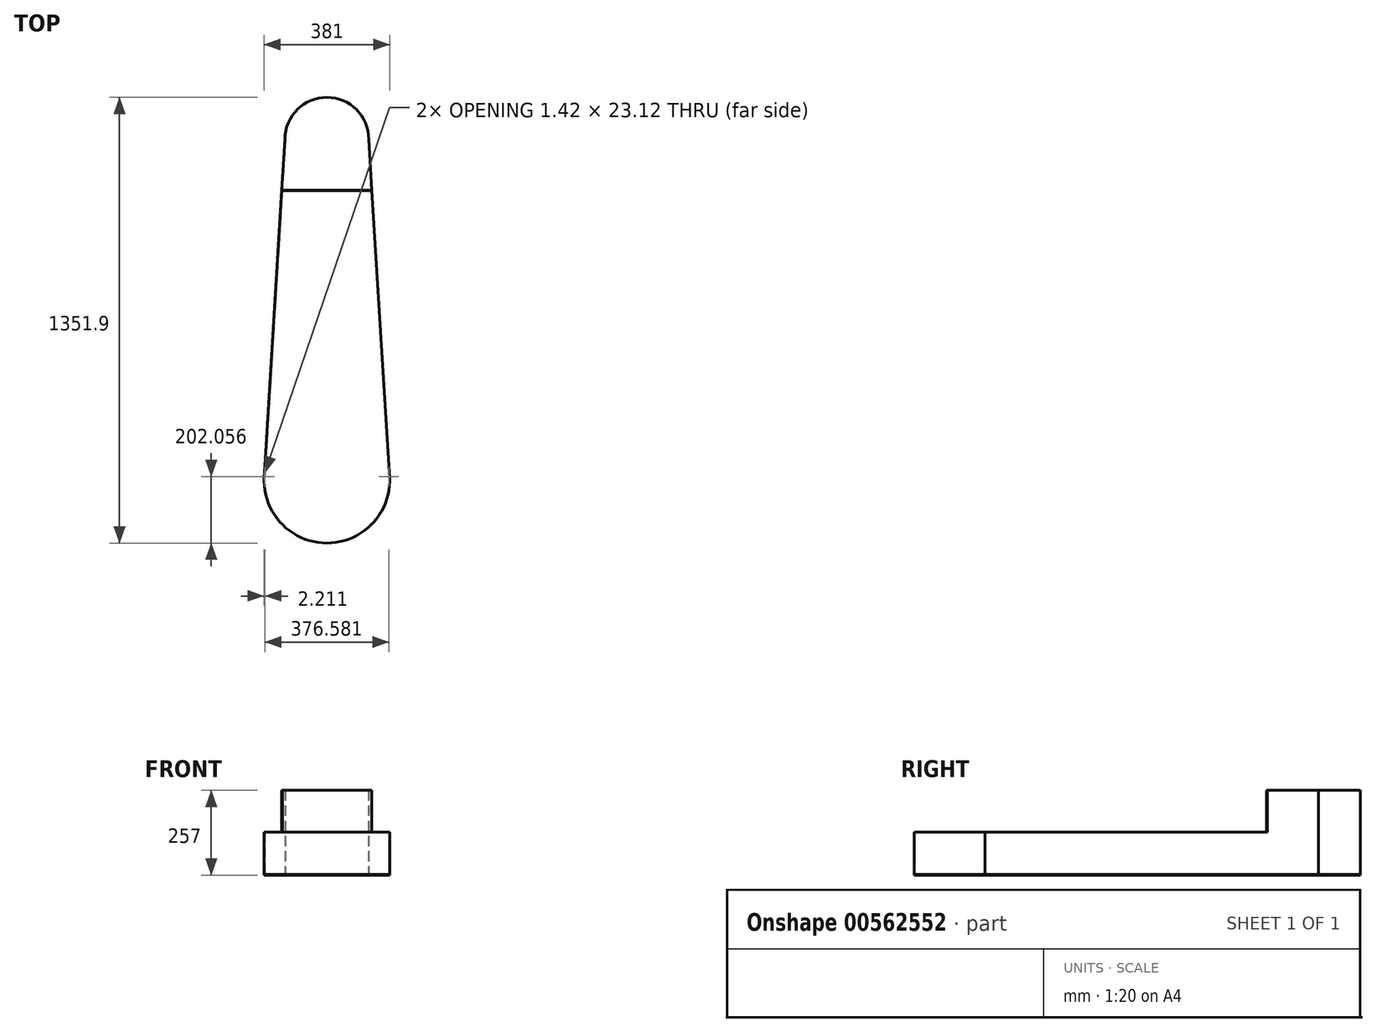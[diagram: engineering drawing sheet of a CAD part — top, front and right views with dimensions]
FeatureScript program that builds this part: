
annotation { "Feature Type Name" : "Feature", "Feature Type Description" : "" }
export const myFeature = defineFeature(function(context is Context, id is Id, definition is map)
    precondition{}
    {
        {
            var Q0;
            Q0=qCreatedBy(makeId("Top.planeOp"),FACE);
            var sketch = newSketch(context, id + "F0", { "sketchPlane" : qUnion([Q0])});
            skArc(sketch, "E0", {"start": v(142.28, 32.75) * mm, "mid": v(15.97, 172.96) * mm, "end": v(-110.34, 32.75) * mm});
            skArc(sketch, "E1", {"start": v(-170.7, -950.41) * mm, "mid": v(15.97, -1178.94) * mm, "end": v(202.64, -950.41) * mm});
            skLineSegment(sketch, "E2", {"start": v(-111.03, 45.96) * mm, "end": v(-174.53, -988.44) * mm});
            skLineSegment(sketch, "E3", {"start": v(142.97, 45.96) * mm, "end": v(206.47, -988.44) * mm});
            skArc(sketch, "E4", {"start": v(141.47, 45.96) * mm, "mid": v(15.97, 171.46) * mm, "end": v(-109.53, 45.96) * mm});
            skArc(sketch, "E5", {"start": v(-171.6, -965.33) * mm, "mid": v(15.97, -1177.44) * mm, "end": v(203.55, -965.33) * mm});
            skLineSegment(sketch, "E6", {"start": v(141.47, 45.96) * mm, "end": v(204.97, -988.44) * mm});
            skLineSegment(sketch, "E7", {"start": v(-109.53, 45.96) * mm, "end": v(-173.03, -988.44) * mm});
            skCircle(sketch, "E8", {"center": v(15.97, 45.96) * mm, "radius": 96.01 * mm});
            skCircle(sketch, "E9", {"center": v(15.97, -988.44) * mm, "radius": 149.65 * mm});
            skLineSegment(sketch, "E10", {"start": v(-120.54, -109.06) * mm, "end": v(-119.04, -109.06) * mm});
            skLineSegment(sketch, "E11", {"start": v(150.99, -109.06) * mm, "end": v(152.48, -108.97) * mm});
            skSolve(sketch);
        }
        {
            var Q0;
            {var subQ0=sQuery(id+"F0.wireOp",EDGE,"E4");Q0=makeQuery(id+"F0.imprint","IMPRINT",FACE,{"disambiguationData":[TD([[makeQuery(id+"F0.imprint","IMPRINT",EDGE,{"derivedFrom":subQ0}),-1.0]])]});}
            var Q1;
            {var subQ5=sQuery(id+"F0.wireOp",EDGE,"E10");Q1=makeQuery(id+"F0.imprint","IMPRINT",FACE,{"disambiguationData":[TD([[makeQuery(id+"F0.imprint","IMPRINT",EDGE,{"derivedFrom":subQ5}),1.0]])]});}
            var Q2;
            {var subQ5=sQuery(id+"F0.wireOp",EDGE,"E11");Q2=makeQuery(id+"F0.imprint","IMPRINT",FACE,{"disambiguationData":[TD([[makeQuery(id+"F0.imprint","IMPRINT",EDGE,{"derivedFrom":subQ5}),1.0]])]});}
            extrude(context, id + "F1", {"entities" : qUnion([Q0, Q1, Q2]), "depth" : 254 * mm, "offsetDistance" : 25.4 * mm});
        }
        {
            var Q0;
            Q0 = qSketchRegion(id + "F0", true);
            extrude(context, id + "F2", {"entities" : qUnion([Q0]), "operationType" : NewBodyOperationType.ADD, "depth" : 127 * mm, "offsetDistance" : 25.4 * mm});
        }
        {
            var Q0;
            Q0 = qSketchRegion(id + "F0", true);
            var Q1;
            {var subQ4=sQuery(id+"F0.wireOp",EDGE,"E4");Q1=makeQuery(id+"F0.imprint","IMPRINT",FACE,{"disambiguationData":[TD([[makeQuery(id+"F0.imprint","IMPRINT",EDGE,{"derivedFrom":subQ4}),1.0]])]});}
            var Q2;
            Q2=makeQuery(id+"F0.imprint","IMPRINT",FACE,{"disambiguationData":[TD([[makeQuery(id+"F0.imprint","IMPRINT",EDGE,{"derivedFrom":sQuery(id+"F0.wireOp",EDGE,"E9")}),1.0]])]});
            var Q3;
            Q3=makeQuery(id+"F0.imprint","IMPRINT",FACE,{"disambiguationData":[TD([[makeQuery(id+"F0.imprint","IMPRINT",EDGE,{"derivedFrom":sQuery(id+"F0.wireOp",EDGE,"E8")}),1.0]])]});
            extrude(context, id + "F3", {"entities" : qUnion([Q0, Q1, Q2, Q3]), "oppositeDirection" : true, "depth" : 1.5 * mm, "offsetDistance" : 25.4 * mm});
        }
        {
            var Q0;
            Q0=makeQuery(id+"F1.opExtrude","CAP_FACE",FACE,{"disambiguationData":[OSD([sQuery(id+"F0.wireOp",EDGE,"E0"),sQuery(id+"F0.wireOp",EDGE,"E2"),sQuery(id+"F0.wireOp",EDGE,"E3"),sQuery(id+"F0.wireOp",EDGE,"E4"),sQuery(id+"F0.wireOp",EDGE,"E6"),sQuery(id+"F0.wireOp",EDGE,"E7"),sQuery(id+"F0.wireOp",EDGE,"E10"),sQuery(id+"F0.wireOp",EDGE,"E11")])],"isStart":false});
            var sketch = newSketch(context, id + "F4", { "sketchPlane" : qUnion([Q0])});
            skLineSegment(sketch, "E12", {"start": v(-119.04, -109.06) * mm, "end": v(152.48, -108.97) * mm});
            skSolve(sketch);
        }
        {
            var Q0;
            {var subQ4=makeQuery(id+"F1.opExtrude","CAP_EDGE",EDGE,{"disambiguationData":[OSD([sQuery(id+"F0.wireOp",EDGE,"E4")])],"isStart":false});Q0=makeQuery(id+"F4.imprint","IMPRINT",FACE,{"disambiguationData":[TD([[makeQuery(id+"F4.imprint","IMPRINT",EDGE,{"derivedFrom":subQ4}),1.0]])]});}
            var Q1;
            Q1=makeQuery(id+"F4.imprint","IMPRINT",FACE,{"disambiguationData":[TD([[makeQuery(id+"F4.imprint","IMPRINT",EDGE,{"derivedFrom":makeQuery(id+"F1.opExtrude","CAP_EDGE",EDGE,{"disambiguationData":[OSD([sQuery(id+"F0.wireOp",EDGE,"E0")])],"isStart":false})}),1.0]])]});
            extrude(context, id + "F5", {"entities" : qUnion([Q0, Q1]), "operationType" : NewBodyOperationType.ADD, "depth" : 1.5 * mm, "offsetDistance" : 25.4 * mm});
        }
        {
            var Q0;
            Q0=makeQuery(id+"F2.opExtrude","CAP_FACE",FACE,{"disambiguationData":[OSD([sQuery(id+"F0.wireOp",EDGE,"E0"),sQuery(id+"F0.wireOp",EDGE,"E1"),sQuery(id+"F0.wireOp",EDGE,"E2"),sQuery(id+"F0.wireOp",EDGE,"E3"),sQuery(id+"F0.wireOp",EDGE,"E4"),sQuery(id+"F0.wireOp",EDGE,"E5"),sQuery(id+"F0.wireOp",EDGE,"E6"),sQuery(id+"F0.wireOp",EDGE,"E7")])],"isStart":false});
            var sketch = newSketch(context, id + "F6", { "sketchPlane" : qUnion([Q0])});
            skLineSegment(sketch, "E13", {"start": v(-120.54, -109.06) * mm, "end": v(152.48, -108.97) * mm});
            skSolve(sketch);
        }
        {
            var Q0;
            Q0=makeQuery(id+"F6.imprint","IMPRINT",FACE,{"disambiguationData":[TD([[makeQuery(id+"F6.imprint","IMPRINT",EDGE,{"derivedFrom":sQuery(id+"F6.wireOp",EDGE,"E13")}),-1.0]])]});
            var Q1;
            {var subQ3=sQuery(id+"F0.wireOp",EDGE,"E1");Q1=makeQuery(id+"F6.imprint","IMPRINT",FACE,{"disambiguationData":[TD([[makeQuery(id+"F6.imprint","IMPRINT",EDGE,{"derivedFrom":makeQuery(id+"F2.opExtrude","CAP_EDGE",EDGE,{"disambiguationData":[OSD([subQ3])],"isStart":false})}),1.0]])]});}
            extrude(context, id + "F7", {"entities" : qUnion([Q0, Q1]), "operationType" : NewBodyOperationType.ADD, "depth" : 1.5 * mm, "offsetDistance" : 25.4 * mm});
        }
        {
            var Q0;
            {var subQ0=sQuery(id+"F0.wireOp",EDGE,"E10");Q0=makeQuery(id+"F5.boolean.opBoolean","MERGE",FACE,{"derivedFrom":[makeQuery(id+"F1.opExtrude","SWEPT_FACE",FACE,{"disambiguationData":[OSD([subQ0])]}),makeQuery(id+"F5.opExtrude","SWEPT_FACE",FACE,{"disambiguationData":[OSD([subQ0])]})]});}
            var sketch = newSketch(context, id + "F8", { "sketchPlane" : qUnion([Q0])});
            skLineSegment(sketch, "E14.bottom", {"start": v(-120.54, 128.5) * mm, "end": v(-120.54, 128.5) * mm});
            skLineSegment(sketch, "E14.top", {"start": v(-120.54, 255.5) * mm, "end": v(-120.54, 255.5) * mm});
            skPoint(sketch, "E15.end.orphan", {"position": v(152.48, 255.5) * mm});
            skLineSegment(sketch, "E16.bottom", {"start": v(-120.54, 255.5) * mm, "end": v(152.48, 255.5) * mm});
            skLineSegment(sketch, "E16.top", {"start": v(-120.54, 128.5) * mm, "end": v(152.48, 128.5) * mm});
            skLineSegment(sketch, "E16.left", {"start": v(-120.54, 255.5) * mm, "end": v(-120.54, 128.5) * mm});
            skLineSegment(sketch, "E16.right", {"start": v(152.48, 255.5) * mm, "end": v(152.48, 128.5) * mm});
            skSolve(sketch);
        }
        {
            var Q0;
            {var subQ0=sQuery(id+"F8.wireOp",EDGE,"E16.right");Q0=makeQuery(id+"F8.imprint","IMPRINT",FACE,{"disambiguationData":[TD([[makeQuery(id+"F8.imprint","IMPRINT",EDGE,{"derivedFrom":subQ0}),-1.0]])]});}
            extrude(context, id + "F9", {"entities" : qUnion([Q0]), "depth" : 1.5 * mm, "offsetDistance" : 25.4 * mm});
        }
    });
